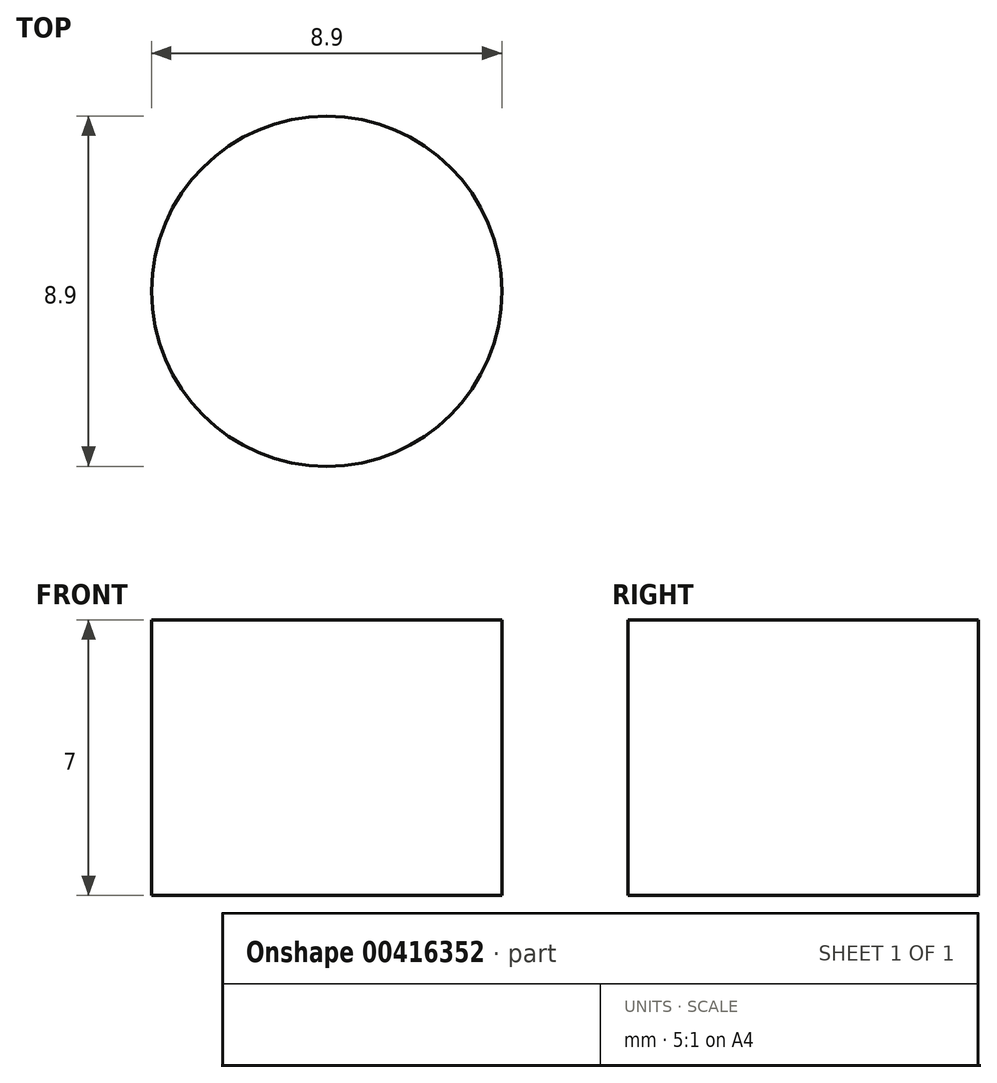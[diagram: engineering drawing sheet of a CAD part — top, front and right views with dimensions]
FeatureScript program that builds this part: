
annotation { "Feature Type Name" : "Feature", "Feature Type Description" : "" }
export const myFeature = defineFeature(function(context is Context, id is Id, definition is map)
    precondition{}
    {
        {
            var Q0;
            Q0=qCreatedBy(makeId("Top.planeOp"),FACE);
            var sketch = newSketch(context, id + "F0", { "sketchPlane" : qUnion([Q0])});
            skCircle(sketch, "E0", {"center": v(0, 0) * mm, "radius": 4.45 * mm});
            skSolve(sketch);
        }
        {
            var Q0;
            Q0 = qSketchRegion(id + "F0", true);
            extrude(context, id + "F1", {"entities" : qUnion([Q0]), "depth" : 7 * mm});
        }
    });
